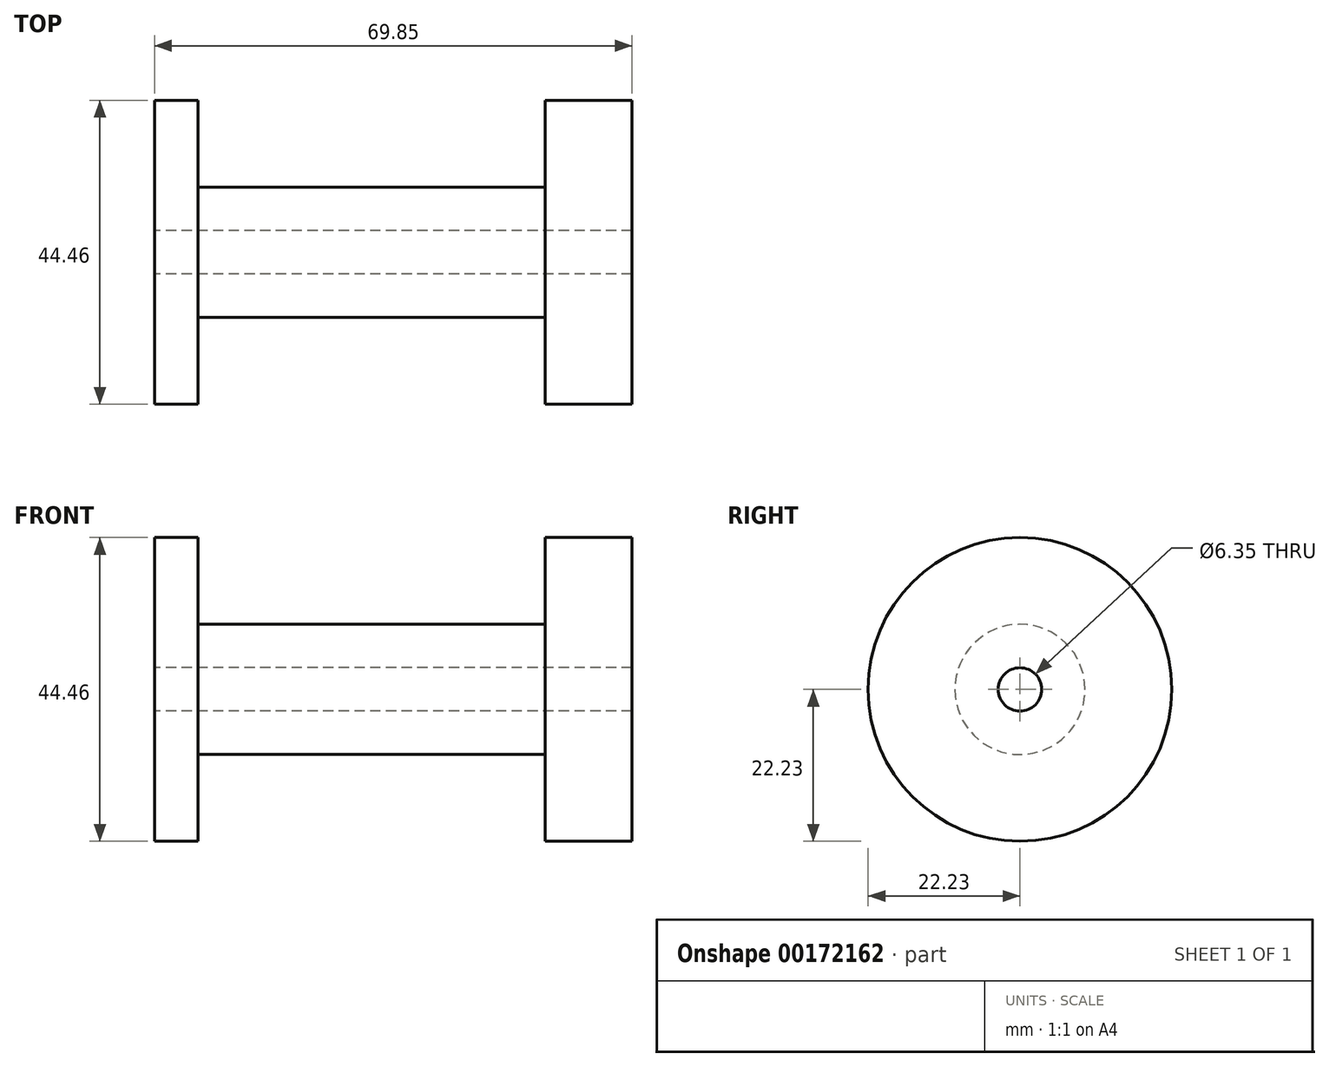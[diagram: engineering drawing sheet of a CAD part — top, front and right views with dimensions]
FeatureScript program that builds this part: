
annotation { "Feature Type Name" : "Feature", "Feature Type Description" : "" }
export const myFeature = defineFeature(function(context is Context, id is Id, definition is map)
    precondition{}
    {
        {
            var Q0;
            Q0=qCreatedBy(makeId("Front.planeOp"),FACE);
            var sketch = newSketch(context, id + "F0", { "sketchPlane" : qUnion([Q0])});
            skLineSegment(sketch, "E0", {"start": v(-57.07, 0) * mm, "end": v(54.4, 0) * mm, "construction": true});
            skLineSegment(sketch, "E1", {"start": v(-22.69, 3.17) * mm, "end": v(-22.69, 22.22) * mm});
            skLineSegment(sketch, "E2", {"start": v(-22.69, 22.22) * mm, "end": v(-16.34, 22.22) * mm});
            skLineSegment(sketch, "E3", {"start": v(-16.34, 22.22) * mm, "end": v(-16.34, 9.53) * mm});
            skLineSegment(sketch, "E4", {"start": v(-16.34, 9.52) * mm, "end": v(34.46, 9.53) * mm});
            skLineSegment(sketch, "E5", {"start": v(34.46, 9.53) * mm, "end": v(34.46, 22.22) * mm});
            skLineSegment(sketch, "E6", {"start": v(34.46, 22.22) * mm, "end": v(47.16, 22.22) * mm});
            skLineSegment(sketch, "E7", {"start": v(47.16, 22.22) * mm, "end": v(47.16, 3.18) * mm});
            skLineSegment(sketch, "E8", {"start": v(47.16, 3.18) * mm, "end": v(-22.69, 3.17) * mm});
            skSolve(sketch);
        }
        {
            var Q0;
            Q0 = qSketchRegion(id + "F0", true);
            var Q1;
            Q1=sQuery(id+"F0.wireOp",EDGE,"E0");
            revolve(context, id + "F1", {"entities" : qUnion([Q0]), "axis" : qUnion([Q1]), "revolveType" : RevolveType.FULL});
        }
    });
